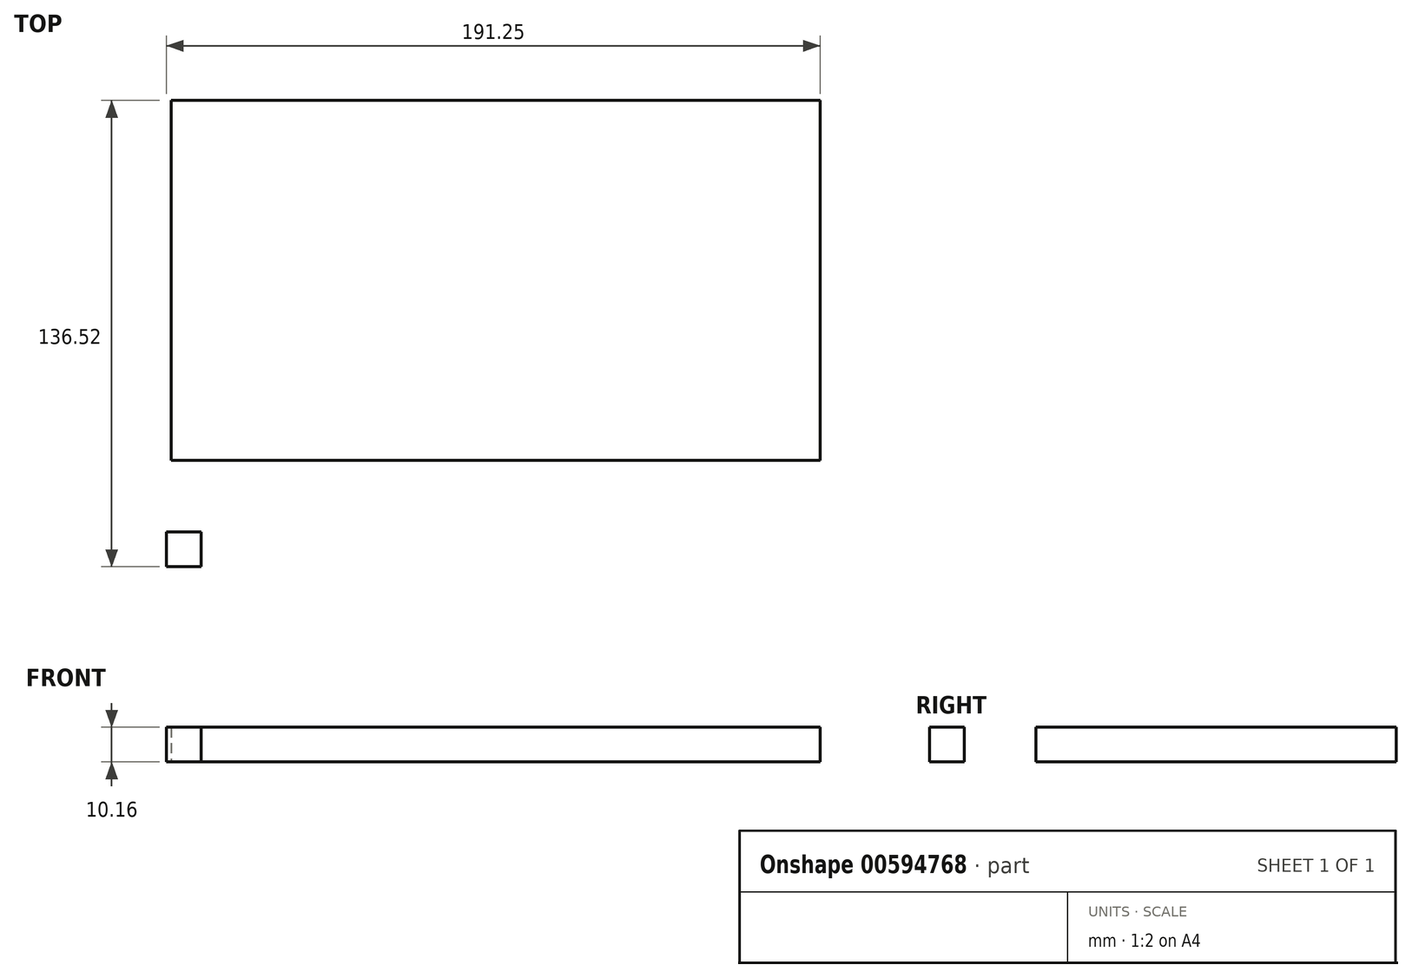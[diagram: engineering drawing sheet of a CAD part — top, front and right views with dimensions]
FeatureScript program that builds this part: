
annotation { "Feature Type Name" : "Feature", "Feature Type Description" : "" }
export const myFeature = defineFeature(function(context is Context, id is Id, definition is map)
    precondition{}
    {
        {
            var Q0;
            Q0=qCreatedBy(makeId("Top.planeOp"),FACE);
            var sketch = newSketch(context, id + "F0", { "sketchPlane" : qUnion([Q0])});
            skLineSegment(sketch, "E0.bottom", {"start": v(-218.32, 62.56) * mm, "end": v(-28.45, 62.56) * mm});
            skLineSegment(sketch, "E0.top", {"start": v(-218.32, -42.85) * mm, "end": v(-28.45, -42.85) * mm});
            skLineSegment(sketch, "E0.left", {"start": v(-218.32, 62.56) * mm, "end": v(-218.32, -42.85) * mm});
            skLineSegment(sketch, "E0.right", {"start": v(-28.45, 62.56) * mm, "end": v(-28.45, -42.85) * mm});
            skLineSegment(sketch, "E1.bottom", {"start": v(-219.7, -63.8) * mm, "end": v(-209.54, -63.8) * mm});
            skLineSegment(sketch, "E1.top", {"start": v(-219.7, -73.96) * mm, "end": v(-209.54, -73.96) * mm});
            skLineSegment(sketch, "E1.left", {"start": v(-219.7, -63.8) * mm, "end": v(-219.7, -73.96) * mm});
            skLineSegment(sketch, "E1.right", {"start": v(-209.54, -63.8) * mm, "end": v(-209.54, -73.96) * mm});
            skSolve(sketch);
        }
        {
            var Q0;
            Q0 = qSketchRegion(id + "F0", true);
            extrude(context, id + "F1", {"entities" : qUnion([Q0]), "depth" : 10.16 * mm, "offsetDistance" : 25.4 * mm});
        }
        {
            var Q0;
            Q0=sQuery(id+"F0.wireOp",EDGE,"E1.top");
            var Q1;
            Q1=sQuery(id+"F0.wireOp",EDGE,"E1.left");
            var Q2;
            Q2=sQuery(id+"F0.wireOp",EDGE,"E1.right");
            var Q3;
            Q3=sQuery(id+"F0.wireOp",EDGE,"E1.bottom");
            extrude(context, id + "F2", {"bodyType" : ToolBodyType.SURFACE, "surfaceEntities" : qUnion([Q0, Q1, Q2, Q3]), "depth" : 137.16 * mm, "offsetDistance" : 25.4 * mm});
        }
    });
